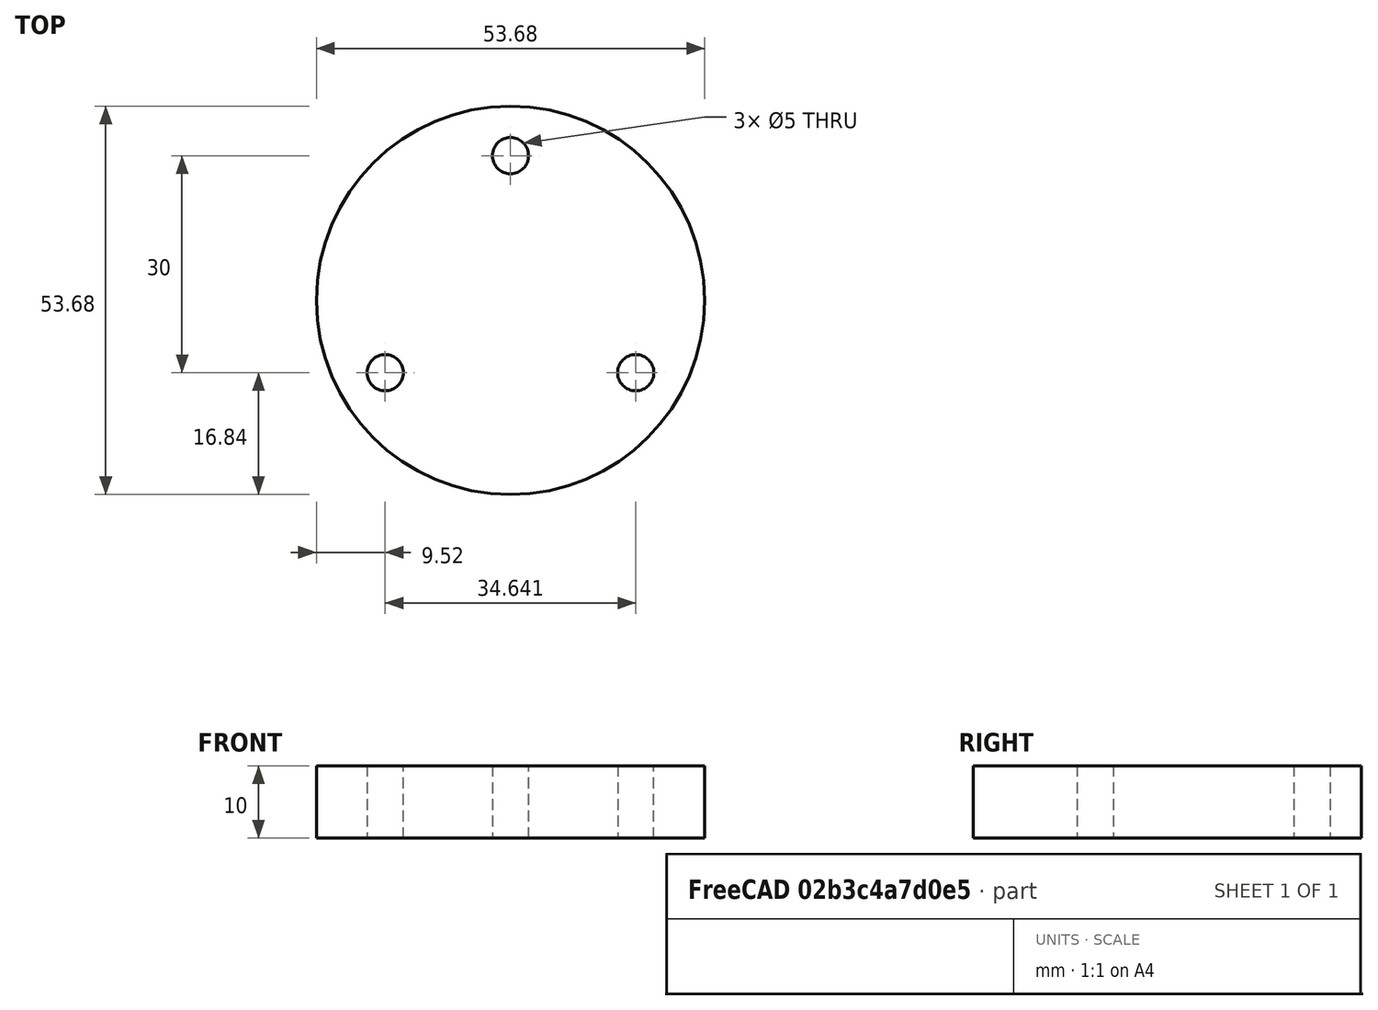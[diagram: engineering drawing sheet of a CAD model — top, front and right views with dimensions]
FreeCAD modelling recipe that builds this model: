
FCSTD DOCUMENT  (FreeCAD 0.19R24276 (Git))
Label: blin_1
License: All rights reserved
LicenseURL: http://en.wikipedia.org/wiki/All_rights_reserved
objects: Sketcher::SketchObject×1, PartDesign::Pad×1, PartDesign::Body×1
note: 4 computed .brp shape members not serialized (recipe doc carries the construction recipe); baked Part::Feature solids carry a one-line shape summary decoded from their .brp

FEATURE [Sketcher::SketchObject] Sketch
  FullyConstrained = false
  MapMode = 5
  Support = -> [XY_Plane]
  sketch-geometry (8):
    g0: Circle CenterX=0 CenterY=0 CenterZ=0 NormalX=0 NormalY=0 NormalZ=1 AngleXU=0 Radius=26.8376
    g1: LineSegment StartX=-17.3205 StartY=-10 StartZ=0 EndX=17.3205 EndY=-10 EndZ=0
    g2: LineSegment StartX=17.3205 StartY=-10 StartZ=0 EndX=0 EndY=20 EndZ=0
    g3: LineSegment StartX=0 StartY=20 StartZ=0 EndX=-17.3205 EndY=-10 EndZ=0
    g4: Circle CenterX=0 CenterY=0 CenterZ=0 NormalX=0 NormalY=0 NormalZ=1 AngleXU=0 Radius=20
    g5: Circle CenterX=0 CenterY=20 CenterZ=0 NormalX=0 NormalY=0 NormalZ=1 AngleXU=0 Radius=2.5
    g6: Circle CenterX=-17.3205 CenterY=-10 CenterZ=0 NormalX=0 NormalY=0 NormalZ=1 AngleXU=0 Radius=2.5
    g7: Circle CenterX=17.3205 CenterY=-10 CenterZ=0 NormalX=0 NormalY=0 NormalZ=1 AngleXU=0 Radius=2.5
  constraints (18):
    c: Coincident(g0,g-1)
    c: Coincident(g1,g2)
    c: Coincident(g2,g3)
    c: Coincident(g3,g1)
    c: Equal(g1,g2)
    c: Equal(g1,g3)
    c: PointOnObject(g1,g4)
    c: PointOnObject(g2,g4)
    c: PointOnObject(g3,g4)
    c: PointOnObject(g2,g-2)
    c: Coincident(g4,g0)
    c: DistanceY(g0,g2) = 20
    c: Coincident(g5,g2)
    c: Coincident(g6,g1)
    c: Coincident(g7,g1)
    c: Equal(g5,g6)
    c: Equal(g6,g7)
    c: Diameter(g5) = 5
FEATURE [PartDesign::Pad] Pad
  Direction = (1,1,1)
  Length = 10
  Length2 = 100
  Profile = -> Sketch
  Type = 0
FEATURE [PartDesign::Body] Body
  Group = -> [Sketch,Pad]
  Origin = -> Origin
  Tip = -> Pad
